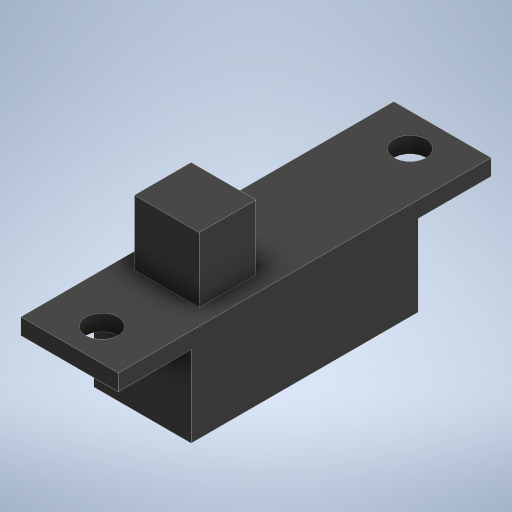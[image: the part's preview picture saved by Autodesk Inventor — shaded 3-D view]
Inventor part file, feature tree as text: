
AUTODESK INVENTOR PART (.ipt)
format: ipt  version: 2024.2 (Build 282272000, 272)  size: 256,000 bytes
history: native  units: mm
features: extrude x3, sketch x3
ambient origin geometry x8: Origin, YZ Plane, XZ Plane, XY Plane, X Axis, Y Axis, Z Axis, Center Point
bodies: Solid1 (feature_tree)
feature tree (6):
  extrude  "Extrusion1"  Depth=23.0mm
  extrude  "Extrusion2"  Depth=2.0mm
  extrude  "Extrusion3"  Depth=4.0mm
  sketch  "Sketch1"  dims[d0=6.0mm d1=23.0mm]
  sketch  "Sketch2"  dims[d2=2.0mm d3=2.0mm]
  sketch  "Sketch3"  dims[d4=19.0mm d5=2.0mm d6=3.0mm d7=1.0mm d8=0.0mm d9=14.0mm d10=4.5mm d11=5.0mm d12=0.0mm d13=4.0mm d14=3.5mm d15=1.0mm d16=6.0mm d17=4.0mm d18=0.0mm]
